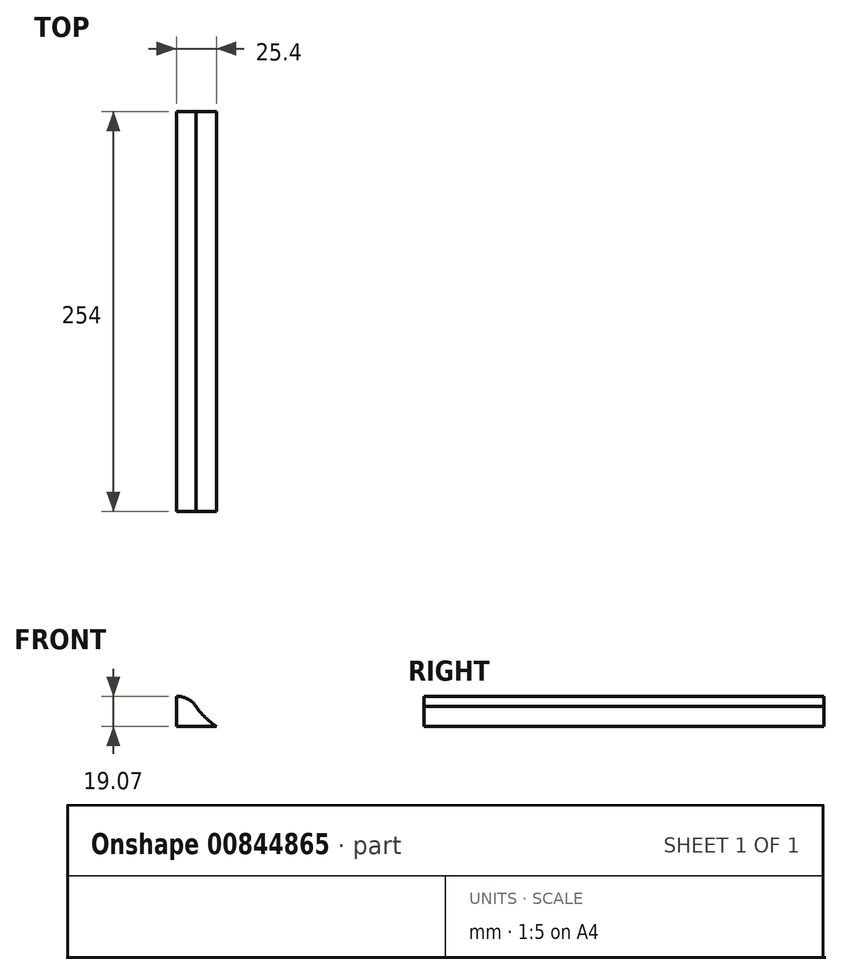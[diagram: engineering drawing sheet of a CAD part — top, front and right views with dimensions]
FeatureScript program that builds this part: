
annotation { "Feature Type Name" : "Feature", "Feature Type Description" : "" }
export const myFeature = defineFeature(function(context is Context, id is Id, definition is map)
    precondition{}
    {
        {
            var Q0;
            Q0=qCreatedBy(makeId("Front.planeOp"),FACE);
            var sketch = newSketch(context, id + "F0", { "sketchPlane" : qUnion([Q0])});
            skLineSegment(sketch, "E0", {"start": v(0, 0) * mm, "end": v(25.4, 0) * mm});
            skLineSegment(sketch, "E1", {"start": v(0, 0) * mm, "end": v(0, 19.05) * mm});
            skArc(sketch, "E2", {"start": v(12.54, 12.64) * mm, "mid": v(7.14, 17.54) * mm, "end": v(0, 19.05) * mm});
            skArc(sketch, "E3", {"start": v(12.54, 12.64) * mm, "mid": v(18.4, 5.73) * mm, "end": v(25.4, 0) * mm});
            skSolve(sketch);
        }
        {
            var Q0;
            Q0=makeQuery(id+"F0.imprint","IMPRINT",FACE,{"disambiguationData":[TD([[makeQuery(id+"F0.imprint","IMPRINT",EDGE,{"derivedFrom":sQuery(id+"F0.wireOp",EDGE,"E0")}),1.0]])]});
            extrude(context, id + "F1", {"entities" : qUnion([Q0]), "depth" : 254 * mm, "offsetDistance" : 25.4 * mm});
        }
    });
